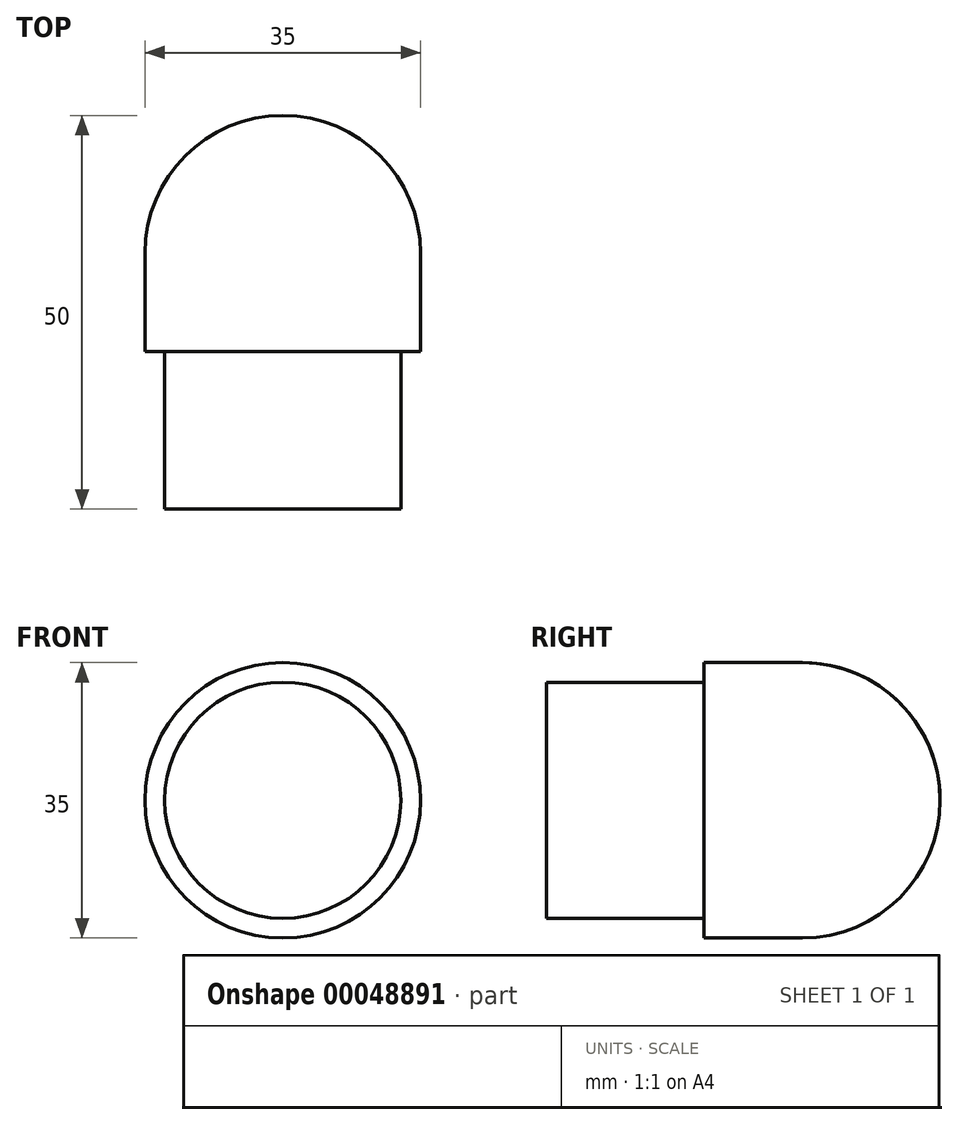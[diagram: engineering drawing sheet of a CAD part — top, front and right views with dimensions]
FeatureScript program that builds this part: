
annotation { "Feature Type Name" : "Feature", "Feature Type Description" : "" }
export const myFeature = defineFeature(function(context is Context, id is Id, definition is map)
    precondition{}
    {
        {
            var Q0;
            Q0=qCreatedBy(makeId("Right.planeOp"),FACE);
            var sketch = newSketch(context, id + "F0", { "sketchPlane" : qUnion([Q0])});
            skLineSegment(sketch, "E0", {"start": v(-102.44, 9.5) * mm, "end": v(-102.44, 24.5) * mm});
            skLineSegment(sketch, "E1", {"start": v(-102.44, 24.5) * mm, "end": v(-82.44, 24.5) * mm});
            skLineSegment(sketch, "E2", {"start": v(-82.44, 24.5) * mm, "end": v(-82.44, 27) * mm});
            skLineSegment(sketch, "E3", {"start": v(-82.44, 27) * mm, "end": v(-69.94, 27) * mm});
            skLineSegment(sketch, "E4", {"start": v(-69.94, 9.5) * mm, "end": v(-102.44, 9.5) * mm});
            skArc(sketch, "E5", {"start": v(-69.94, 27) * mm, "mid": v(-57.57, 21.88) * mm, "end": v(-52.44, 9.5) * mm});
            skLineSegment(sketch, "E6", {"start": v(-69.94, 9.5) * mm, "end": v(-52.44, 9.5) * mm});
            skSolve(sketch);
        }
        {
            var Q0;
            Q0=makeQuery(id+"F0.imprint","IMPRINT",FACE,{"disambiguationData":[TD([[makeQuery(id+"F0.imprint","IMPRINT",EDGE,{"derivedFrom":sQuery(id+"F0.wireOp",EDGE,"E0")}),-1.0]])]});
            var Q1;
            Q1=sQuery(id+"F0.wireOp",EDGE,"E4");
            revolve(context, id + "F1", {"entities" : qUnion([Q0]), "axis" : qUnion([Q1]), "revolveType" : RevolveType.FULL});
        }
    });
